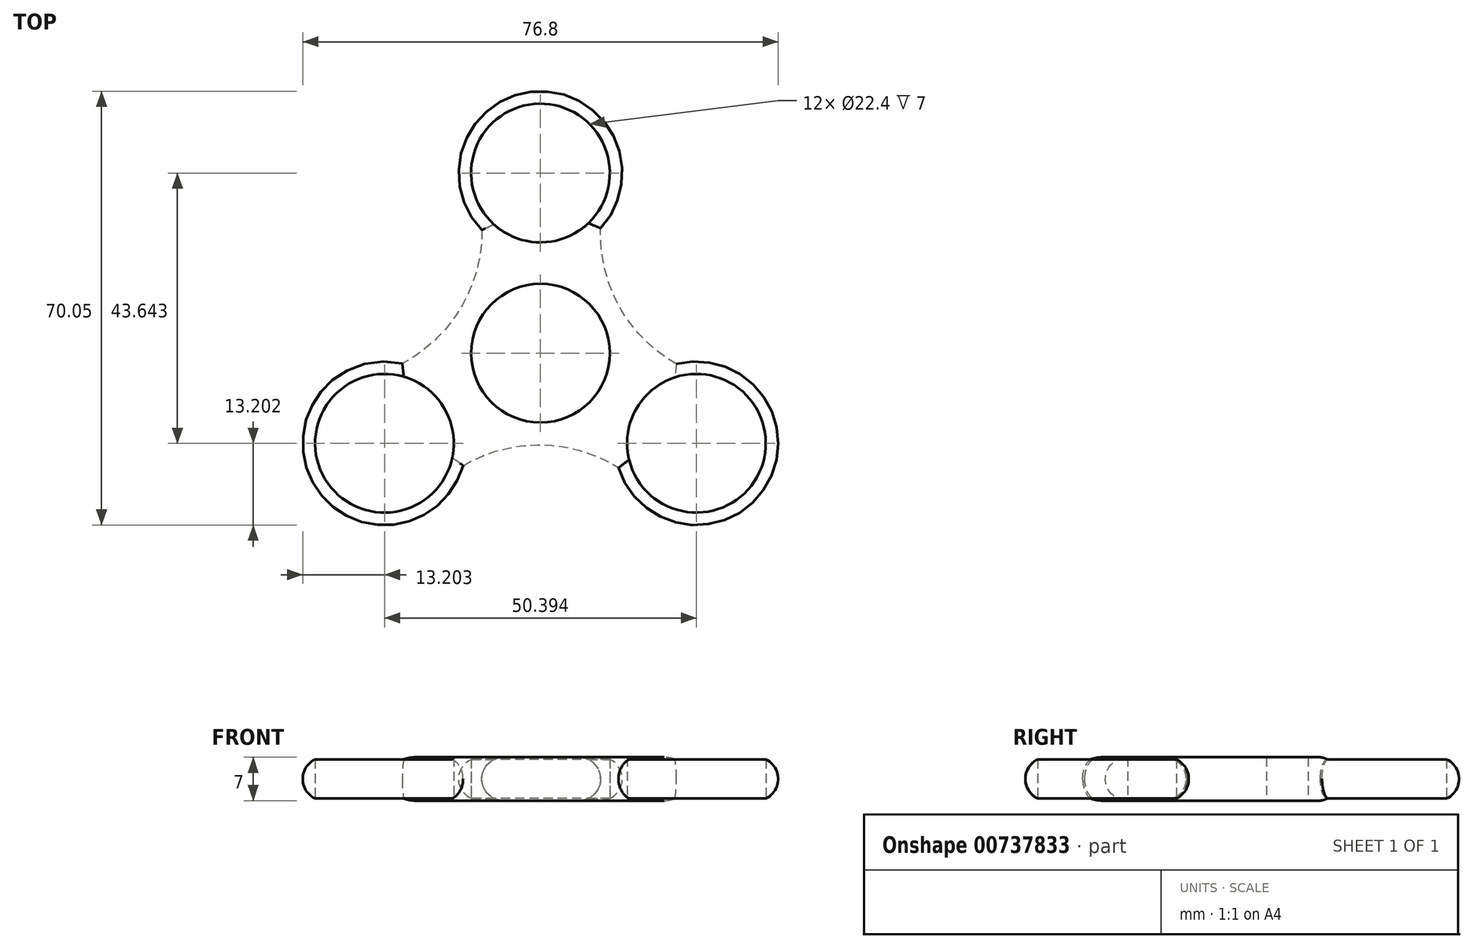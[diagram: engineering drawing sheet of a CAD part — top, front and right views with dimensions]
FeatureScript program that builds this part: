
annotation { "Feature Type Name" : "Feature", "Feature Type Description" : "" }
export const myFeature = defineFeature(function(context is Context, id is Id, definition is map)
    precondition{}
    {
        {
            var Q0;
            Q0=qCreatedBy(makeId("Top.planeOp"),FACE);
            var sketch = newSketch(context, id + "F0", { "sketchPlane" : qUnion([Q0])});
            skCircle(sketch, "E0", {"center": v(0, 0) * mm, "radius": 11.2 * mm});
            skCircle(sketch, "E1", {"center": v(0, 29.1) * mm, "radius": 11.2 * mm});
            skArc(sketch, "E2", {"start": v(9.72, 20.17) * mm, "mid": v(-0.19, 42.3) * mm, "end": v(-9.47, 19.9) * mm});
            skCircle(sketch, "E3.1.0", {"center": v(-25.2, -14.55) * mm, "radius": 11.2 * mm});
            skArc(sketch, "E3.1.1", {"start": v(-22.33, -1.66) * mm, "mid": v(-36.54, -21.3) * mm, "end": v(-12.5, -18.15) * mm});
            skCircle(sketch, "E3.2.0", {"center": v(25.2, -14.55) * mm, "radius": 11.2 * mm});
            skArc(sketch, "E3.2.1", {"start": v(12.6, -18.5) * mm, "mid": v(36.72, -20.99) * mm, "end": v(21.97, -1.75) * mm});
            skArc(sketch, "E4", {"start": v(-22.33, -1.66) * mm, "mid": v(-12.88, 7.32) * mm, "end": v(-9.47, 19.9) * mm});
            skArc(sketch, "E5.1.0", {"start": v(12.6, -18.5) * mm, "mid": v(0.1, -14.81) * mm, "end": v(-12.5, -18.15) * mm});
            skArc(sketch, "E5.2.0", {"start": v(9.72, 20.17) * mm, "mid": v(12.78, 7.5) * mm, "end": v(21.97, -1.75) * mm});
            skPoint(sketch, "E6.orphan", {"position": v(76.2, 76.2) * mm});
            skSolve(sketch);
        }
        {
            var Q0;
            Q0=makeQuery(id+"F0.imprint","IMPRINT",FACE,{"disambiguationData":[TD([[makeQuery(id+"F0.imprint","IMPRINT",EDGE,{"derivedFrom":sQuery(id+"F0.wireOp",EDGE,"E0")}),-1.0]])]});
            extrude(context, id + "F1", {"entities" : qUnion([Q0]), "depth" : 7 * mm, "offsetDistance" : 25 * mm});
        }
        {
            var Q0;
            Q0=makeQuery(id+"F1.opExtrude","CAP_EDGE",EDGE,{"disambiguationData":[OSD([sQuery(id+"F0.wireOp",EDGE,"E4")])],"isStart":false});
            var Q1;
            Q1=makeQuery(id+"F1.opExtrude","CAP_EDGE",EDGE,{"disambiguationData":[OSD([sQuery(id+"F0.wireOp",EDGE,"E2")])],"isStart":false});
            var Q2;
            Q2=makeQuery(id+"F1.opExtrude","CAP_EDGE",EDGE,{"disambiguationData":[OSD([sQuery(id+"F0.wireOp",EDGE,"E5.2.0")])],"isStart":false});
            var Q3;
            Q3=makeQuery(id+"F1.opExtrude","CAP_EDGE",EDGE,{"disambiguationData":[OSD([sQuery(id+"F0.wireOp",EDGE,"E3.2.1")])],"isStart":false});
            var Q4;
            Q4=makeQuery(id+"F1.opExtrude","CAP_EDGE",EDGE,{"disambiguationData":[OSD([sQuery(id+"F0.wireOp",EDGE,"E5.1.0")])],"isStart":false});
            var Q5;
            Q5=makeQuery(id+"F1.opExtrude","CAP_EDGE",EDGE,{"disambiguationData":[OSD([sQuery(id+"F0.wireOp",EDGE,"E3.1.1")])],"isStart":false});
            fillet(context, id + "F2", {"entities" : qUnion([Q0, Q1, Q2, Q3, Q4, Q5]), "radius" : 3.5 * mm, "tangentPropagation" : true, "allowEdgeOverflow" : false});
        }
        {
            var Q0;
            Q0=makeQuery(id+"F1.opExtrude","CAP_EDGE",EDGE,{"disambiguationData":[OSD([sQuery(id+"F0.wireOp",EDGE,"E5.2.0")])],"isStart":true});
            var Q1;
            Q1=makeQuery(id+"F1.opExtrude","CAP_EDGE",EDGE,{"disambiguationData":[OSD([sQuery(id+"F0.wireOp",EDGE,"E4")])],"isStart":true});
            var Q2;
            Q2=makeQuery(id+"F1.opExtrude","CAP_EDGE",EDGE,{"disambiguationData":[OSD([sQuery(id+"F0.wireOp",EDGE,"E5.1.0")])],"isStart":true});
            var Q3;
            Q3=makeQuery(id+"F1.opExtrude","CAP_EDGE",EDGE,{"disambiguationData":[OSD([sQuery(id+"F0.wireOp",EDGE,"E2")])],"isStart":true});
            var Q4;
            Q4=makeQuery(id+"F1.opExtrude","CAP_EDGE",EDGE,{"disambiguationData":[OSD([sQuery(id+"F0.wireOp",EDGE,"E3.2.1")])],"isStart":true});
            var Q5;
            Q5=makeQuery(id+"F1.opExtrude","CAP_EDGE",EDGE,{"disambiguationData":[OSD([sQuery(id+"F0.wireOp",EDGE,"E3.1.1")])],"isStart":true});
            fillet(context, id + "F3", {"entities" : qUnion([Q0, Q1, Q2, Q3, Q4, Q5]), "radius" : 3.5 * mm, "tangentPropagation" : true, "allowEdgeOverflow" : false});
        }
    });
